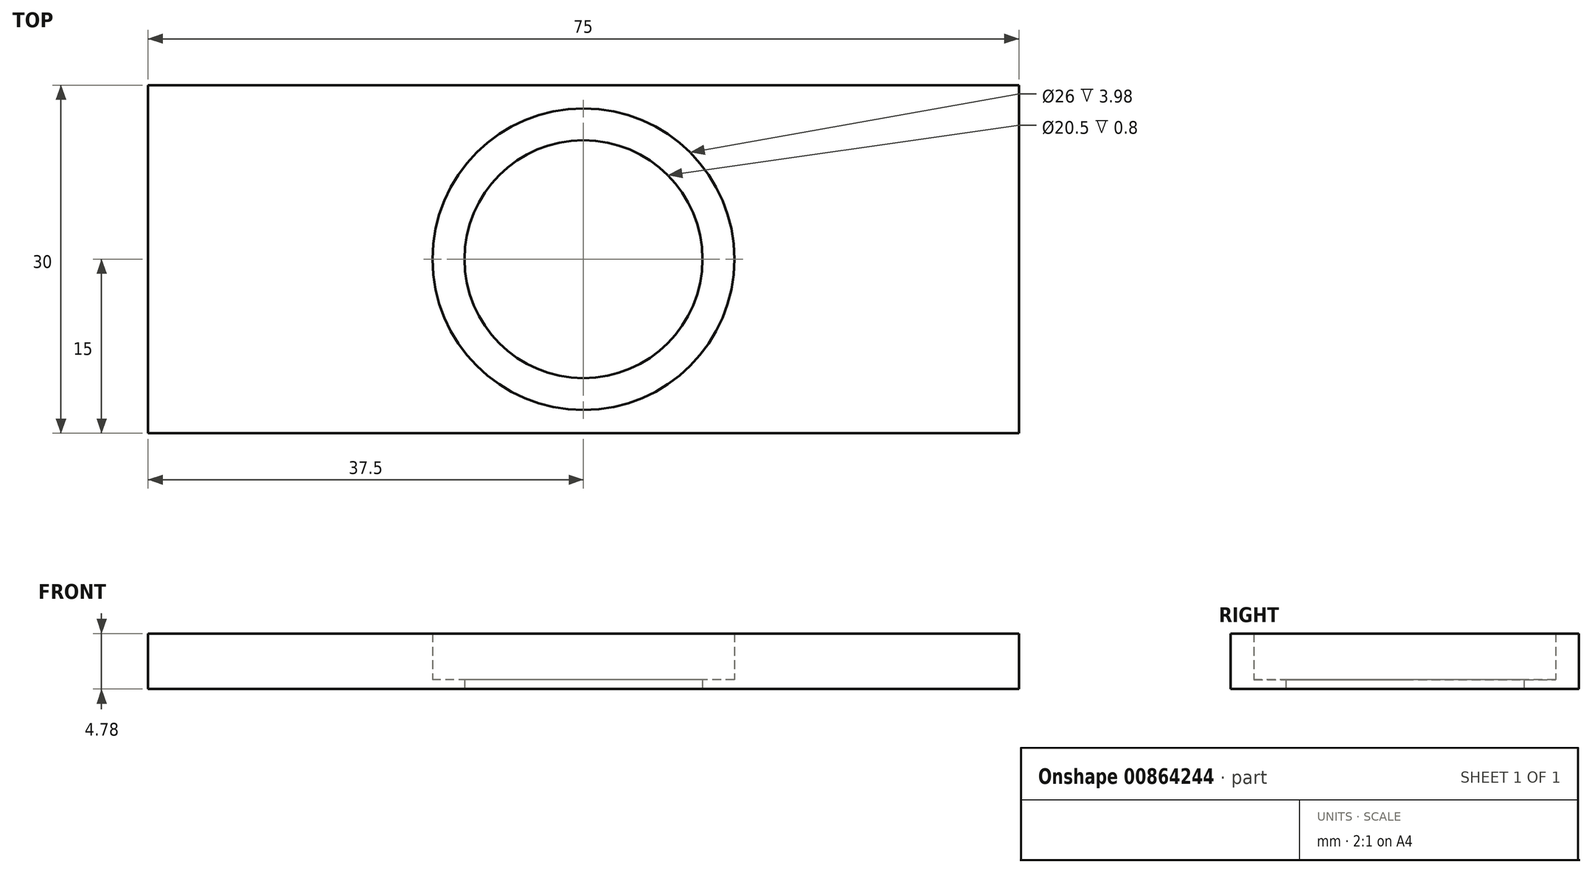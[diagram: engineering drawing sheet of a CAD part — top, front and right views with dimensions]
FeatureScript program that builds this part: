
annotation { "Feature Type Name" : "Feature", "Feature Type Description" : "" }
export const myFeature = defineFeature(function(context is Context, id is Id, definition is map)
    precondition{}
    {
        {
            var Q0;
            Q0=qCreatedBy(makeId("Top.planeOp"),FACE);
            var sketch = newSketch(context, id + "F0", { "sketchPlane" : qUnion([Q0])});
            skLineSegment(sketch, "E0.bottom", {"start": v(-37.5, 15) * mm, "end": v(37.5, 15) * mm});
            skLineSegment(sketch, "E0.top", {"start": v(-37.5, -15) * mm, "end": v(37.5, -15) * mm});
            skLineSegment(sketch, "E0.left", {"start": v(-37.5, 15) * mm, "end": v(-37.5, -15) * mm});
            skLineSegment(sketch, "E0.right", {"start": v(37.5, 15) * mm, "end": v(37.5, -15) * mm});
            skCircle(sketch, "E1", {"center": v(0, 0) * mm, "radius": 10.25 * mm});
            skCircle(sketch, "E2", {"center": v(0, 0) * mm, "radius": 13 * mm});
            skSolve(sketch);
        }
        {
            var Q0;
            Q0=makeQuery(id+"F0.imprint","IMPRINT",FACE,{"disambiguationData":[TD([[makeQuery(id+"F0.imprint","IMPRINT",EDGE,{"derivedFrom":sQuery(id+"F0.wireOp",EDGE,"E0.bottom")}),-1.0]])]});
            var Q1;
            Q1=sQuery(id+"F0.wireOp",EDGE,"E2");
            var Q2;
            Q2=sQuery(id+"F0.wireOp",EDGE,"E0.bottom");
            var Q3;
            Q3=sQuery(id+"F0.wireOp",EDGE,"E0.left");
            var Q4;
            Q4=sQuery(id+"F0.wireOp",EDGE,"E0.top");
            var Q5;
            Q5=sQuery(id+"F0.wireOp",EDGE,"E0.right");
            extrude(context, id + "F1", {"entities" : qUnion([Q0]), "surfaceEntities" : qUnion([Q1, Q2, Q3, Q4, Q5]), "depth" : 4.78 * mm, "offsetDistance" : 25 * mm});
        }
        {
            var Q0;
            Q0=makeQuery(id+"F0.imprint","IMPRINT",FACE,{"disambiguationData":[TD([[makeQuery(id+"F0.imprint","IMPRINT",EDGE,{"derivedFrom":sQuery(id+"F0.wireOp",EDGE,"E1")}),-1.0]])]});
            extrude(context, id + "F2", {"entities" : qUnion([Q0]), "operationType" : NewBodyOperationType.ADD, "depth" : 0.8 * mm, "offsetDistance" : 25 * mm});
        }
    });
